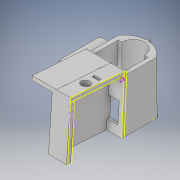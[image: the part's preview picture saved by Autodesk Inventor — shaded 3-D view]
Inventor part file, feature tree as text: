
AUTODESK INVENTOR PART (.ipt)
format: ipt  version: 2018 (Build 220112000, 112)  size: 433,152 bytes
history: native  units: in
note: dims shown in document units (in); Inventor stores cm internally (conversion verified against a paired STEP export)
features: extrude x10, sketch x10, projected_geometry x8, other x4, fillet x2
ambient origin geometry x8: Origin, YZ Plane, XZ Plane, XY Plane, X Axis, Y Axis, Z Axis, Center Point
bodies: Body1 (feature_tree)
feature tree (34):
  other  "Back"
  other  "Front Plane"
  extrude  "Bottom"  Depth=0.15in
  extrude  "FrontExtend"  Depth=0.65in
  extrude  "Battery Holder"  Depth=0.15in
  extrude  "Ir Reciever holder"  TaperAngle=0.0deg  [1 undecoded]
  extrude  "IR Reciever/ LED Cutout"  Depth=0.1in
  extrude  "Double LED Holder"  Depth=0.95in
  extrude  "Double LED Cutout"  TaperAngle=180.0deg  [1 undecoded]
  fillet  "Fillet2"  Radius=0.1418in
  extrude  "Extrusion11"  Depth=0.142in
  extrude  "Extrusion12"  Depth=0.1in
  sketch  "Sketch17"  dims[d59=0.142in d60=0.1in d61=0.1in]
  fillet  "Fillet4"  Radius=0.1in
  extrude  "Extrusion13"  Depth=0.15in TaperAngle=0.0deg
  other  "Front"
  other  "BottomSketch"
  sketch  "Sketch8"  dims[d2=0.15in d7=0.421in]
  sketch  "Sketch9"  dims[d23=0.65in d25=0.7163in]
  projected_geometry  "Projected Loop1"
  sketch  "Sketch10"  dims[d37=0.5575in d38=0.15in]
  projected_geometry  "Projected Loop2"
  sketch  "Sketch11"  dims[d39=0.15in d42=0.0in d43=90.0deg d44=0.0in d45=90.0deg]
  projected_geometry  "Projected Loop3"
  sketch  "Sketch13"  dims[d50=0.0in d51=0.1in]
  sketch  "Sketch14"  dims[d52=0.95in d53=0.95in]
  projected_geometry  "Projected Loop4"
  sketch  "Sketch15"  dims[d54=0.421in d55=180.0deg d56=0.1418in]
  projected_geometry  "Projected Loop5"
  sketch  "Sketch16"  dims[d57=0.142in d58=0.142in]
  projected_geometry  "Projected Loop6"
  projected_geometry  "Projected Loop7"
  sketch  "Sketch18"  dims[d62=0.1in d63=0.0in d66=0.15in d67=0.0in d69=0.15in d72=0.75in d73=0.15in d74=2.0in d75=0.0in d76=2.0in d77=0.0in d83=0.1in d84=0.25in d85=0.8in d86=0.325in d87=0.15in d88=0.0in d89=1.5in d90=0.15in d91=0.5in d92=0.0in d93=0.325in d94=0.325in d95=0.25in d96=0.25in d97=0.25in d98=0.0in d100=0.125in d101=0.15in d102=1.25in d103=1.5in d104=0.3in d105=0.4in d106=0.15in d107=0.15in d108=1.55in d109=0.0in d115=1.2in d116=0.15in d117=0.518in d118=0.0in d119=1.5in d120=0.325in d121=0.4in d122=0.25in d123=0.125in d124=0.4in d125=0.75in d126=0.35in d127=0.2in d128=0.0in]
  projected_geometry  "Projected Loop8"
note: 2 required parameter values undecoded (feature->parameter linkage not recoverable at this tier; creation-order binding heuristic only, values carry confidence <= 0.55)
